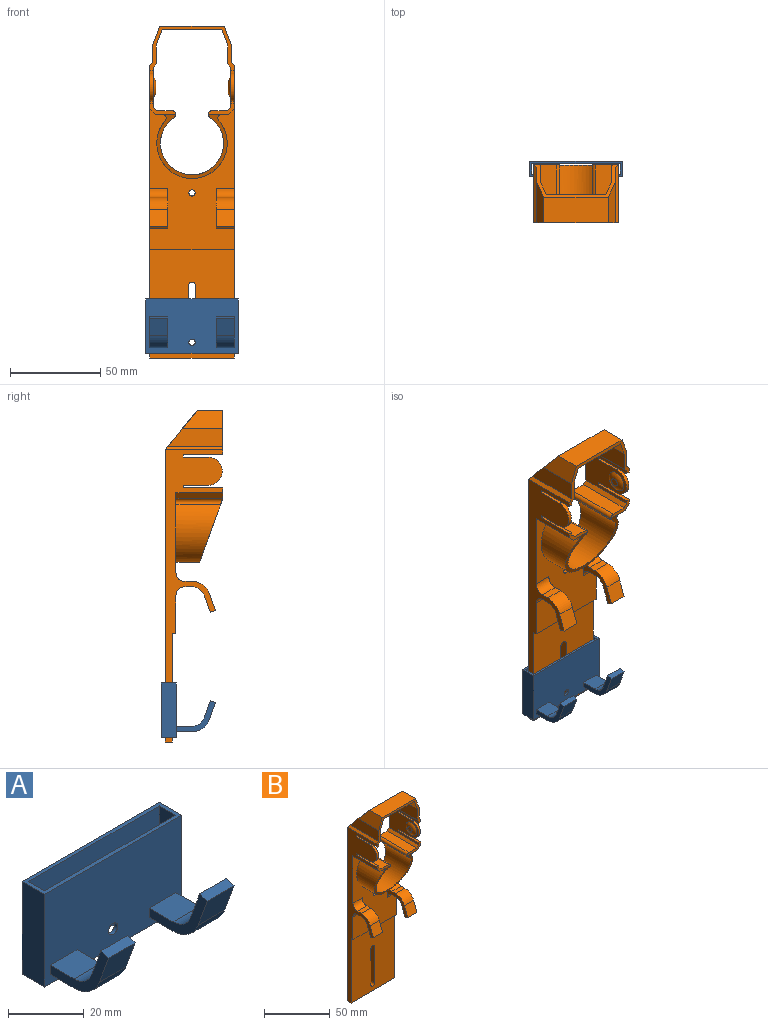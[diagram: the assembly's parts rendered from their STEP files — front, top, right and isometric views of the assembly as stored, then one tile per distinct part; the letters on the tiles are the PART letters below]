
ASSEMBLY  parts=2 mates=1
PART A: 30 faces, bbox 51.4x30.1x30 mm
  f0: plane 51.4x30mm, normal (0,-1,0), area 1472.4mm2, adj f5,f6,f7,f8,f9,f10,f11,f18
  f1: plane 49x30mm, normal (0,1,0), area 1460.4mm2, adj f2,f6,f7,f17,f29
  f2: plane 30x6mm, normal (-1,0,0), area 180mm2, adj f1,f3,f6,f7
  f3: plane 49x30mm, normal (0,-1,0), area 1460.4mm2, adj f2,f6,f7,f17,f28
  f4: plane 51.4x30mm, normal (0,1,0), area 1532.4mm2, adj f5,f6,f7,f18,f28
  f5: plane 30x8.4mm, normal (1,0,0), area 252mm2, adj f0,f4,f6,f7
  f6: plane 51.4x8.4mm, normal (0,0,1), area 137.8mm2, adj f0,f1,f2,f3,f4,f5,f17,f18
  f7: plane 51.4x8.4mm, normal (0,0,-1), area 137.8mm2, adj f0,f1,f2,f3,f4,f5,f17,f18
  f8: plane 10x8.9mm, normal (0,0,-1), area 89mm2, adj f0,f10,f11,f12
  f9: plane 10x8.9mm, normal (0,0,1), area 89mm2, adj f0,f10,f11,f13
  f10: plane 21.75x17.1mm, normal (-1,0,0), area 88.1mm2, adj f0,f8,f9,f12,f13,f14,f15,f16
  f11: plane 21.75x17.1mm, normal (1,0,0), area 88.1mm2, adj f0,f8,f9,f12,f13,f14,f15,f16
  f12: cylinder r=10mm len=10mm, axis (1,0,0), area 122.2mm2, adj f8,f10,f11,f16
  f13: cylinder r=7mm len=10mm, axis (1,0,0), area 85.5mm2, adj f9,f10,f11,f14
  f14: plane 10x9.49mm, normal (0,0.94,0.34), area 101mm2, adj f10,f11,f13,f15
  f15: plane 10x2.82mm, normal (0,-0.34,0.94), area 30mm2, adj f10,f11,f14,f16
  f16: plane 10x9.49mm, normal (0,-0.94,-0.34), area 101mm2, adj f10,f11,f12,f15
  f17: plane 30x6mm, normal (1,0,0), area 180mm2, adj f1,f3,f6,f7
  f18: plane 30x8.4mm, normal (-1,0,0), area 252mm2, adj f0,f4,f6,f7
  f19: plane 10x8.9mm, normal (0,0,-1), area 89mm2, adj f0,f21,f22,f23
  f20: plane 10x8.9mm, normal (0,0,1), area 89mm2, adj f0,f21,f22,f24
  f21: plane 21.75x17.1mm, normal (1,0,0), area 88.1mm2, adj f0,f19,f20,f23,f24,f25,f26,f27
  f22: plane 21.75x17.1mm, normal (-1,0,0), area 88.1mm2, adj f0,f19,f20,f23,f24,f25,f26,f27
  f23: cylinder r=10mm len=10mm, axis (-1,0,0), area 122.2mm2, adj f19,f21,f22,f27
  f24: cylinder r=7mm len=10mm, axis (-1,0,0), area 85.5mm2, adj f20,f21,f22,f25
  f25: plane 10x9.49mm, normal (0,0.94,0.34), area 101mm2, adj f21,f22,f24,f26
  f26: plane 10x2.82mm, normal (0,-0.34,0.94), area 30mm2, adj f21,f22,f25,f27
  f27: plane 10x9.49mm, normal (0,-0.94,-0.34), area 101mm2, adj f21,f22,f23,f26
  f28: cylinder r=1.75mm len=3.5mm, axis (0,-1,0), area 13.2mm2, adj f3,f4
  f29: cylinder r=1.75mm len=3.5mm, axis (0,-1,0), area 13.2mm2, adj f0,f1
PART B: 87 faces, bbox 47x32x184 mm
  f0: plane 162.03x47mm, normal (0,1,0), area 5397.9mm2, adj f9,f11,f12,f13,f17,f19,f20,f24
  f1: plane 60x47mm, normal (0,-1,0), area 2671.4mm2, adj f11,f18,f24,f54,f82,f83,f84,f85
  f2: plane 32x1.8mm, normal (0.71,0,0.71), area 79.6mm2, adj f3,f11,f16,f36
  f3: plane 30.53x10.04mm, normal (1,0,0), area 265.1mm2, adj f2,f4,f16,f36
  f4: plane 22.3x10.14mm, normal (0.94,0,0.35), area 196.6mm2, adj f3,f5,f16,f36
  f5: plane 35.77x14mm, normal (0,0,1), area 500.8mm2, adj f4,f16,f36,f49
  f6: plane 33x15.64mm, normal (0,0,-1), area 516.1mm2, adj f7,f16,f36,f50
  f7: plane 22.6x8.5mm, normal (-0.94,0,-0.35), area 173.7mm2, adj f6,f8,f16,f36
  f8: plane 31.2x10.5mm, normal (-1,0,0), area 282.5mm2, adj f7,f9,f16,f36
  f9: plane 32x1.8mm, normal (-0.71,0,-0.71), area 80.9mm2, adj f0,f8,f12,f16,f36
  f10: plane 14.5x5.85mm, normal (0,-1,0), area 32.8mm2, adj f11,f12,f17,f19,f20,f21,f22,f25
  f11: plane 162.03x32mm, normal (1,0,0), area 1476.3mm2, adj f0,f1,f2,f10,f16,f18,f22,f23
  f12: plane 32x22.2mm, normal (-1,0,0), area 510.9mm2, adj f0,f9,f10,f16,f19,f27,f28,f29
  f13: cylinder r=17.5mm len=35mm, axis (0,1,0), area 2199.5mm2, adj f0,f17,f26,f57
  f14: cylinder r=19.5mm len=39mm, axis (0,1,0), area 1579.5mm2, adj f15,f23,f26,f56
  f15: cylinder r=2mm len=26mm, axis (0,1,0), area 116.3mm2, adj f14,f21,f23,f26
  f16: plane 47x24.65mm, normal (0,-1,0), area 168.9mm2, adj f2,f3,f4,f5,f6,f7,f8,f9
  f17: cylinder r=2mm len=32mm, axis (0,1,0), area 60mm2, adj f0,f10,f13,f25,f26
  f18: plane 47x2mm, normal (0,0,-1), area 94mm2, adj f1,f11,f23,f54
  f19: plane 32x2mm, normal (-0.71,0,0.71), area 90.5mm2, adj f0,f10,f12,f20
  f20: plane 32x8.5mm, normal (0,0,1), area 272mm2, adj f0,f10,f19,f25
  f21: plane 26x4.01mm, normal (0,0,-1), area 104.3mm2, adj f10,f15,f22,f23
  f22: plane 26x3.17mm, normal (0.71,0,-0.71), area 116.6mm2, adj f10,f11,f21,f23
  f23: plane 78.17x47mm, normal (0,-1,0), area 2113.9mm2, adj f11,f14,f15,f18,f21,f22,f44,f45
  f24: plane 47x4mm, normal (0,0,-1), area 188mm2, adj f0,f1,f11,f54
  f25: cylinder r=2mm len=32mm, axis (0,-1,0), area 98.9mm2, adj f0,f10,f17,f20
  f26: plane 39x35.5mm, normal (0,-0.94,-0.34), area 214.6mm2, adj f10,f13,f14,f15,f17,f53,f56,f57
  f27: plane 22x2mm, normal (0,0,1), area 44mm2, adj f10,f11,f12,f31
  f28: plane 22x2mm, normal (0,0,-1), area 44mm2, adj f11,f12,f16,f29
  f29: plane 2x1.5mm, normal (0,-1,0), area 3mm2, adj f11,f12,f28,f30
  f30: plane 14x2mm, normal (0,0,1), area 28mm2, adj f11,f12,f29,f32
  f31: plane 2x1.5mm, normal (0,-1,0), area 3mm2, adj f11,f12,f27,f33
  f32: cylinder r=7.75mm len=15.5mm, axis (-1,0,0), area 48.7mm2, adj f11,f12,f30,f33
  f33: plane 14x2mm, normal (0,0,-1), area 28mm2, adj f11,f12,f31,f32
  f34: plane 4.36x4.36mm, normal (-1,0,0), area 14.9mm2, adj f35
  f35: torus R=2.18mm, axis (1,0,0), area 101.6mm2, adj f12,f34
  f36: plane 47x21.97mm, normal (0,0.77,0.63), area 203.6mm2, adj f0,f2,f3,f4,f5,f6,f7,f8
  f37: cylinder r=7mm len=10mm, axis (1,0,0), area 85.5mm2, adj f11,f38,f43,f44
  f38: plane 10x4.1mm, normal (0,0,-1), area 41mm2, adj f11,f37,f44,f45
  f39: plane 10x4.1mm, normal (0,0,1), area 41mm2, adj f11,f40,f44,f46
  f40: cylinder r=10mm len=10mm, axis (1,0,0), area 122.2mm2, adj f11,f39,f41,f44
  f41: plane 10x9.49mm, normal (0,-0.94,0.34), area 101mm2, adj f11,f40,f42,f44
  f42: plane 10x2.82mm, normal (0,-0.34,-0.94), area 30mm2, adj f11,f41,f43,f44
  f43: plane 10x9.49mm, normal (0,0.94,-0.34), area 101mm2, adj f11,f37,f42,f44
  f44: plane 22.1x21.95mm, normal (-1,0,0), area 99.5mm2, adj f23,f37,f38,f39,f40,f41,f42,f43
  f45: cylinder r=5mm len=10mm, axis (-1,0,0), area 78.5mm2, adj f11,f23,f38,f44
  f46: cylinder r=5mm len=10mm, axis (-1,0,0), area 78.5mm2, adj f11,f23,f39,f44
  f47: plane 32x1.8mm, normal (-0.71,0,0.71), area 79.6mm2, adj f16,f36,f48,f54
  f48: plane 30.53x10.04mm, normal (-1,0,0), area 265.1mm2, adj f16,f36,f47,f49
  f49: plane 22.3x10.14mm, normal (-0.94,0,0.35), area 196.6mm2, adj f5,f16,f36,f48
  f50: plane 22.6x8.5mm, normal (0.94,0,-0.35), area 173.7mm2, adj f6,f16,f36,f51
  f51: plane 31.2x10.5mm, normal (1,0,0), area 282.5mm2, adj f16,f36,f50,f52
  f52: plane 32x1.8mm, normal (0.71,0,-0.71), area 80.9mm2, adj f0,f16,f36,f51,f55
  f53: plane 14.5x5.85mm, normal (0,-1,0), area 32.8mm2, adj f26,f54,f55,f57,f58,f59,f60,f61
  f54: plane 162.03x32mm, normal (-1,0,0), area 1476.3mm2, adj f0,f1,f16,f18,f23,f24,f47,f53
  f55: plane 32x22.2mm, normal (1,0,0), area 510.9mm2, adj f0,f16,f52,f53,f58,f63,f64,f65
  f56: cylinder r=2mm len=26mm, axis (0,1,0), area 116.3mm2, adj f14,f23,f26,f60
  f57: cylinder r=2mm len=32mm, axis (0,1,0), area 60mm2, adj f0,f13,f26,f53,f62
  f58: plane 32x2mm, normal (0.71,0,0.71), area 90.5mm2, adj f0,f53,f55,f59
  f59: plane 32x8.5mm, normal (0,0,1), area 272mm2, adj f0,f53,f58,f62
  f60: plane 26x4.01mm, normal (0,0,-1), area 104.3mm2, adj f23,f53,f56,f61
  f61: plane 26x3.17mm, normal (-0.71,0,-0.71), area 116.6mm2, adj f23,f53,f54,f60
  f62: cylinder r=2mm len=32mm, axis (0,-1,0), area 98.9mm2, adj f0,f53,f57,f59
  f63: plane 22x2mm, normal (0,0,1), area 44mm2, adj f53,f54,f55,f67
  f64: plane 22x2mm, normal (0,0,-1), area 44mm2, adj f16,f54,f55,f65
  f65: plane 2x1.5mm, normal (0,-1,0), area 3mm2, adj f54,f55,f64,f66
  f66: plane 14x2mm, normal (0,0,1), area 28mm2, adj f54,f55,f65,f68
  f67: plane 2x1.5mm, normal (0,-1,0), area 3mm2, adj f54,f55,f63,f69
  f68: cylinder r=7.75mm len=15.5mm, axis (1,0,0), area 48.7mm2, adj f54,f55,f66,f69
  f69: plane 14x2mm, normal (0,0,-1), area 28mm2, adj f54,f55,f67,f68
  f70: plane 4.36x4.36mm, normal (1,0,0), area 14.9mm2, adj f71
  f71: torus R=2.18mm, axis (-1,0,0), area 101.6mm2, adj f55,f70
  f72: cylinder r=7mm len=10mm, axis (-1,0,0), area 85.5mm2, adj f54,f73,f78,f79
  f73: plane 10x4.1mm, normal (0,0,-1), area 41mm2, adj f54,f72,f79,f80
  f74: plane 10x4.1mm, normal (0,0,1), area 41mm2, adj f54,f75,f79,f81
  f75: cylinder r=10mm len=10mm, axis (-1,0,0), area 122.2mm2, adj f54,f74,f76,f79
  f76: plane 10x9.49mm, normal (0,-0.94,0.34), area 101mm2, adj f54,f75,f77,f79
  f77: plane 10x2.82mm, normal (0,-0.34,-0.94), area 30mm2, adj f54,f76,f78,f79
  f78: plane 10x9.49mm, normal (0,0.94,-0.34), area 101mm2, adj f54,f72,f77,f79
  f79: plane 22.1x21.95mm, normal (1,0,0), area 99.5mm2, adj f23,f72,f73,f74,f75,f76,f77,f78
  f80: cylinder r=5mm len=10mm, axis (1,0,0), area 78.5mm2, adj f23,f54,f73,f79
  f81: cylinder r=5mm len=10mm, axis (1,0,0), area 78.5mm2, adj f23,f54,f74,f79
  f82: plane 34x4mm, normal (-1,0,0), area 136mm2, adj f0,f1,f83,f85
  f83: cylinder r=2mm len=4mm, axis (0,-1,0), area 25.1mm2, adj f0,f1,f82,f84
  f84: plane 34x4mm, normal (1,0,0), area 136mm2, adj f0,f1,f83,f85
  f85: cylinder r=2mm len=4mm, axis (0,-1,0), area 25.1mm2, adj f0,f1,f82,f84
  f86: cylinder r=1.75mm len=6mm, axis (0,-1,0), area 66mm2, adj f0,f23
PLACE A t=(-53.03,-36.69,-7.46)mm
PLACE B t=(-53.03,-36.69,-10.16)mm
MATE slider A.f6 <-> B.f24  axis (0,0,1) through (-77.53,-31.69,-96.46)mm
